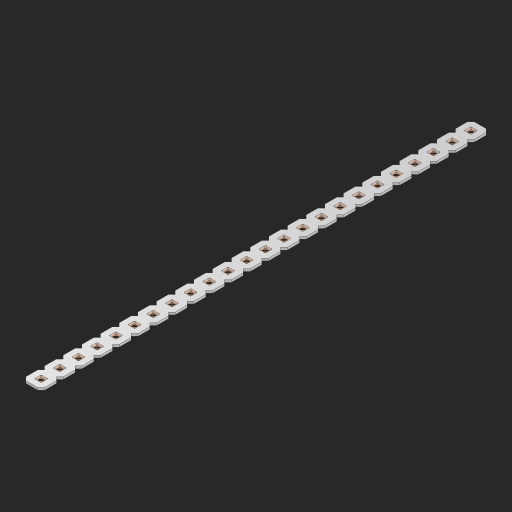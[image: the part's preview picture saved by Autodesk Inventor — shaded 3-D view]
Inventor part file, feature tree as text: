
AUTODESK INVENTOR PART (.ipt)
format: ipt  version: 2023 (Build 270158000, 158)  size: 537,600 bytes
history: native  units: in
note: dims shown in document units (in); Inventor stores cm internally (conversion verified against a paired STEP export)
features: other x25, extrude x23, sketch x2, pattern_linear x1
ambient origin geometry x8: Origin, YZ Plane, XZ Plane, XY Plane, X Axis, Y Axis, Z Axis, Center Point
bodies: Solid1 (feature_tree), Body (feature_tree)
feature tree (51):
  pattern_linear  "Rectangular Pattern1"  Spacing1=0.09in  [1 undecoded]
  sketch  "Sketch1"  dims[d1=0.5in]
  sketch  "Sketch2"  dims[d2=0.182in d3=0.09in d4=0.09in d5=0.09in d6=0.09in d7=0.09in d8=0.09in d9=0.09in d10=0.09in d11=0.02in d13=0.0in d14=0.172in d15=0.0625in d16=0.0in d19=0.5in d22=0.5in]
  other  "Srf1"
  other  "Srf126"
  other  "Srf127"
  other  "Srf128"
  other  "Srf129"
  other  "Srf130"
  other  "Srf131"
  other  "Srf250"
  other  "Srf251"
  other  "Srf252"
  other  "Srf253"
  other  "Srf254"
  other  "Srf255"
  other  "Srf256"
  other  "Srf257"
  other  "Srf258"
  other  "Srf259"
  other  "Srf260"
  other  "Srf261"
  other  "Srf262"
  other  "Srf263"
  other  "Srf264"
  other  "Srf265"
  other  "Srf266"
  other  "Circle"
  extrude  "ExtrusionSrf126"  Depth=0.09in
  extrude  "ExtrusionSrf127"  Depth=0.09in
  extrude  "ExtrusionSrf128"  Depth=0.09in
  extrude  "ExtrusionSrf129"  Depth=0.09in
  extrude  "ExtrusionSrf130"  Depth=0.09in
  extrude  "ExtrusionSrf131"  Depth=0.09in
  extrude  "ExtrusionSrf250"  Depth=0.09in
  extrude  "ExtrusionSrf251"  Depth=0.02in
  extrude  "ExtrusionSrf252"  TaperAngle=0.0deg  [1 undecoded]
  extrude  "ExtrusionSrf253"  Depth=0.5in
  extrude  "ExtrusionSrf254"  Depth=0.0625in TaperAngle=0.0deg
  extrude  "ExtrusionSrf255"  Depth=0.5in
  extrude  "ExtrusionSrf256"  Depth=0.5in
  extrude  "ExtrusionSrf257"  [1 undecoded]
  extrude  "ExtrusionSrf258"  [1 undecoded]
  extrude  "ExtrusionSrf259"  [1 undecoded]
  extrude  "ExtrusionSrf260"  [1 undecoded]
  extrude  "ExtrusionSrf261"  [1 undecoded]
  extrude  "ExtrusionSrf262"  [1 undecoded]
  extrude  "ExtrusionSrf263"  [1 undecoded]
  extrude  "ExtrusionSrf264"  [1 undecoded]
  extrude  "ExtrusionSrf265"  [1 undecoded]
  extrude  "ExtrusionSrf266"  [1 undecoded]
note: 12 required parameter values undecoded (feature->parameter linkage not recoverable at this tier; creation-order binding heuristic only, values carry confidence <= 0.55)
